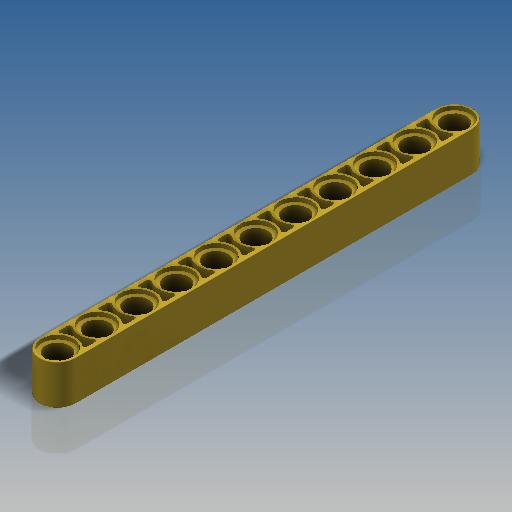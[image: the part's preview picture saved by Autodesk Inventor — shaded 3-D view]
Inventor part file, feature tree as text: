
AUTODESK INVENTOR PART (.ipt)
format: ipt  version: 2018.3 (Build 223284000, 284)  size: 498,688 bytes
history: native  units: mm
features: extrude x3, sketch x2, mirror x1, fillet x1
ambient origin geometry x8: Origin, YZ Plane, XZ Plane, XY Plane, X Axis, Y Axis, Z Axis, Center Point
bodies: Solid1 (feature_tree)
feature tree (7):
  extrude  "Extrusion1"  Depth=7.2mm
  sketch  "Sketch6"  dims[d41=0.8mm d42=0.0mm d43=3.1mm d44=0.0mm d48=80.0mm d49=6.4mm d50=4.8mm d51=8.0mm d52=0.8mm d53=100.0mm d55=8.0mm d56=10.0mm d58=10.0mm d60=0.4mm d61=0.1mm]
  extrude  "Extrusion7"  Depth=3.1mm TaperAngle=0.0deg
  extrude  "Extrusion8"  Depth=0.1mm
  mirror  "Mirror1"
  fillet  "Fillet2"  Radius=6.4mm
  sketch  "Sketch1"  dims[d14=8.0mm d15=0.0mm d32=7.2mm]
